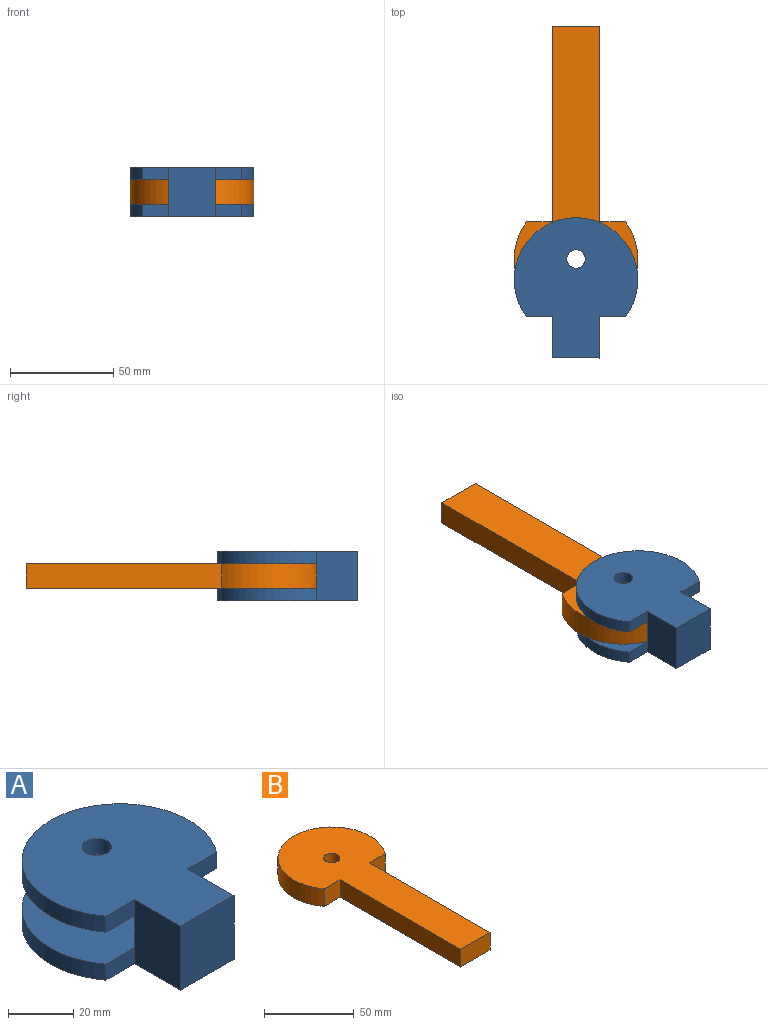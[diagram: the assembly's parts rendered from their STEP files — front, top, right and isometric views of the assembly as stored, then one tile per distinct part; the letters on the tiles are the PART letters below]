
ASSEMBLY  parts=2 mates=1
PART A: 16 faces, bbox 60x68x24 mm
  f0: plane 12.5x6mm, normal (0,-1,0), area 75mm2, adj f2,f5,f10,f13
  f1: plane 12.5x6mm, normal (0,-1,0), area 75mm2, adj f2,f3,f10,f13
  f2: cylinder r=30mm len=60mm, axis (0,0,-1), area 797.1mm2, adj f0,f1,f10,f13
  f3: plane 24x20mm, normal (-1,0,0), area 480mm2, adj f1,f4,f8,f9,f10,f11
  f4: plane 24x23mm, normal (0,-1,0), area 552mm2, adj f3,f5,f9,f10
  f5: plane 24x20mm, normal (1,0,0), area 480mm2, adj f0,f4,f6,f9,f10,f11
  f6: plane 12.5x6mm, normal (0,-1,0), area 75mm2, adj f5,f7,f9,f12
  f7: cylinder r=30mm len=60mm, axis (0,0,-1), area 797.1mm2, adj f6,f8,f9,f12
  f8: plane 12.5x6mm, normal (0,-1,0), area 75mm2, adj f3,f7,f9,f12
  f9: plane 68x60mm, normal (0,0,1), area 2821.3mm2, adj f3,f4,f5,f6,f7,f8,f15
  f10: plane 68x60mm, normal (0,0,-1), area 2821.3mm2, adj f0,f1,f2,f3,f4,f5,f14
  f11: plane 23x12mm, normal (0,1,0), area 276mm2, adj f3,f5,f12,f13
  f12: plane 60x48mm, normal (0,0,-1), area 2361.3mm2, adj f6,f7,f8,f11,f15
  f13: plane 60x48mm, normal (0,0,1), area 2361.3mm2, adj f0,f1,f2,f11,f14
  f14: cylinder r=4.5mm len=9mm, axis (0,0,1), area 169.6mm2, adj f10,f13
  f15: cylinder r=4.5mm len=9mm, axis (0,0,1), area 169.6mm2, adj f9,f12
PART B: 9 faces, bbox 60x143x12 mm
  f0: plane 95x12mm, normal (-1,0,0), area 1140mm2, adj f1,f5,f6,f7
  f1: plane 23x12mm, normal (0,-1,0), area 276mm2, adj f0,f2,f6,f7
  f2: plane 95x12mm, normal (1,0,0), area 1140mm2, adj f1,f3,f6,f7
  f3: plane 12.5x12mm, normal (0,-1,0), area 150mm2, adj f2,f4,f6,f7
  f4: cylinder r=30mm len=60mm, axis (0,0,-1), area 1594.3mm2, adj f3,f5,f6,f7
  f5: plane 12.5x12mm, normal (0,-1,0), area 150mm2, adj f0,f4,f6,f7
  f6: plane 143x60mm, normal (0,0,1), area 4546.3mm2, adj f0,f1,f2,f3,f4,f5,f8
  f7: plane 143x60mm, normal (0,0,-1), area 4546.3mm2, adj f0,f1,f2,f3,f4,f5,f8
  f8: cylinder r=4.5mm len=12mm, axis (0,0,1), area 339.3mm2, adj f6,f7
PLACE A rot(axis=(-0.38,-0.89,-0.25),0deg) t=(184.26,32.17,11.93)mm
PLACE B rot(axis=(0,0,1),180deg) t=(101.93,193.17,17.93)mm
MATE revolute B.f4 <-> A.f14  axis (0,0,1) through (90.43,80.17,29.93)mm
